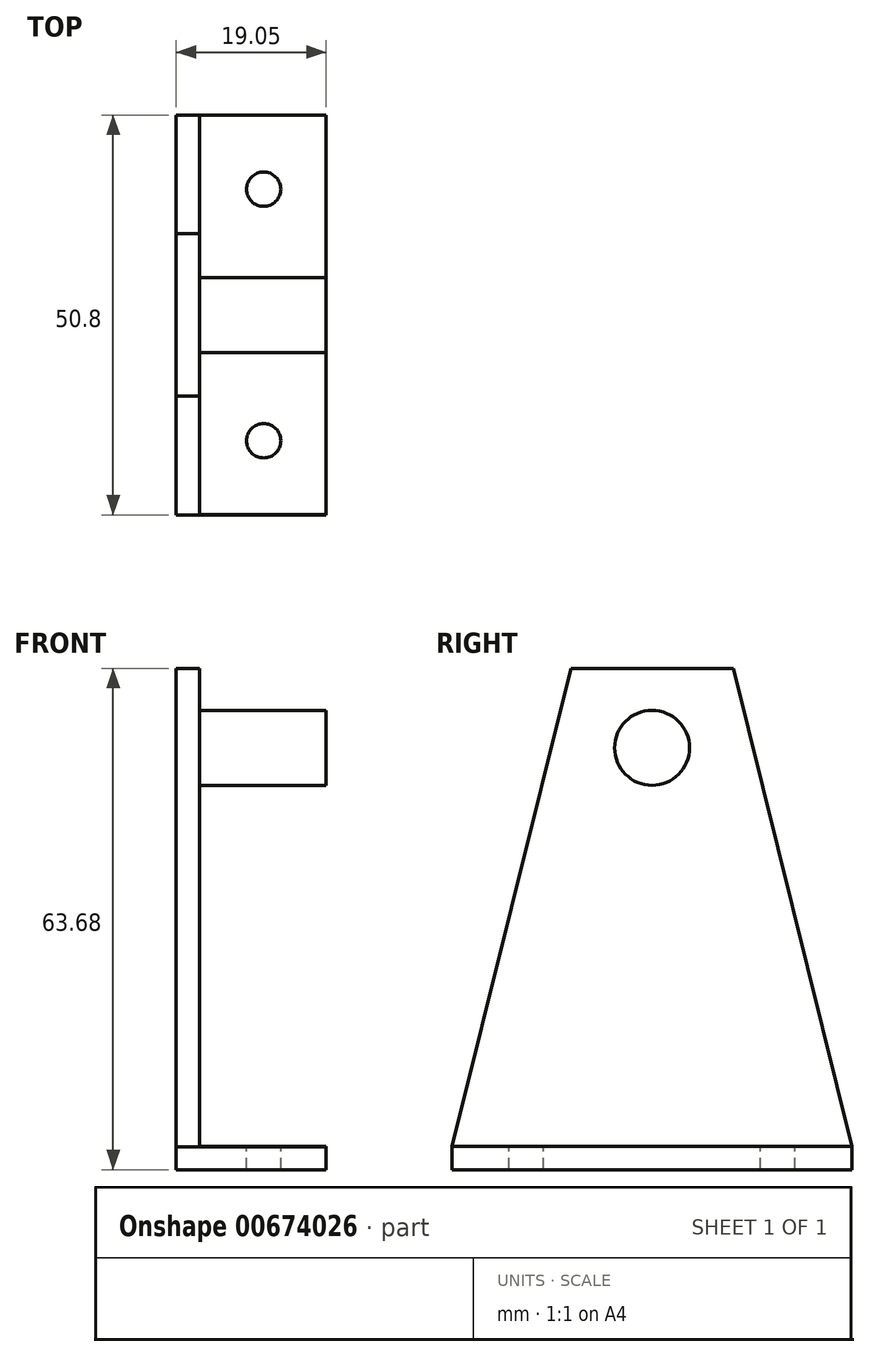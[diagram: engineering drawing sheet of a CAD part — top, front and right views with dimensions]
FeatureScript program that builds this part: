
annotation { "Feature Type Name" : "Feature", "Feature Type Description" : "" }
export const myFeature = defineFeature(function(context is Context, id is Id, definition is map)
    precondition{}
    {
        {
            var Q0;
            Q0=qCreatedBy(makeId("Front.planeOp"),FACE);
            var sketch = newSketch(context, id + "F0", { "sketchPlane" : qUnion([Q0])});
            skLineSegment(sketch, "E0", {"start": v(-9.71, 63.68) * mm, "end": v(-9.71, 0) * mm});
            skLineSegment(sketch, "E1", {"start": v(-9.71, 0) * mm, "end": v(9.34, 0) * mm});
            skLineSegment(sketch, "E2", {"start": v(9.34, 0) * mm, "end": v(9.34, 2.97) * mm});
            skLineSegment(sketch, "E3", {"start": v(9.34, 2.97) * mm, "end": v(-6.74, 2.97) * mm});
            skLineSegment(sketch, "E4", {"start": v(-6.74, 2.97) * mm, "end": v(-6.74, 63.68) * mm});
            skLineSegment(sketch, "E5", {"start": v(-6.74, 63.68) * mm, "end": v(-9.71, 63.68) * mm});
            skLineSegment(sketch, "E6", {"start": v(-6.74, 58.36) * mm, "end": v(9.34, 58.36) * mm});
            skLineSegment(sketch, "E7", {"start": v(9.34, 58.36) * mm, "end": v(9.34, 48.83) * mm});
            skLineSegment(sketch, "E8", {"start": v(9.34, 48.83) * mm, "end": v(-6.74, 48.83) * mm});
            skLineSegment(sketch, "E9", {"start": v(9.34, 53.6) * mm, "end": v(-6.74, 53.6) * mm});
            skSolve(sketch);
        }
        {
            var Q0;
            Q0=makeQuery(id+"F0.imprint","IMPRINT",FACE,{"disambiguationData":[TD([[makeQuery(id+"F0.imprint","IMPRINT",EDGE,{"derivedFrom":sQuery(id+"F0.wireOp",EDGE,"E0")}),1.0]])]});
            extrude(context, id + "F1", {"entities" : qUnion([Q0]), "endBound" : BoundingType.SYMMETRIC, "depth" : 50.8 * mm, "offsetDistance" : 25.4 * mm});
        }
        {
            var Q0;
            {var subQ0=sQuery(id+"F0.wireOp",EDGE,"E6");Q0=makeQuery(id+"F0.imprint","IMPRINT",FACE,{"disambiguationData":[TD([[makeQuery(id+"F0.imprint","IMPRINT",EDGE,{"derivedFrom":subQ0}),-1.0]])]});}
            var Q1;
            Q1=sQuery(id+"F0.wireOp",EDGE,"E9");
            revolve(context, id + "F2", {"operationType" : NewBodyOperationType.ADD, "surfaceOperationType" : NewSurfaceOperationType.ADD, "entities" : qUnion([Q0]), "axis" : qUnion([Q1]), "revolveType" : RevolveType.FULL});
        }
        {
            var Q0;
            Q0=makeQuery(id+"F1.opExtrude","SWEPT_FACE",FACE,{"disambiguationData":[OSD([sQuery(id+"F0.wireOp",EDGE,"E3")])]});
            var sketch = newSketch(context, id + "F3", { "sketchPlane" : qUnion([Q0])});
            skCircle(sketch, "E10", {"center": v(1.4, 15.98) * mm, "radius": 2.18 * mm});
            skCircle(sketch, "E11", {"center": v(1.4, -15.98) * mm, "radius": 2.18 * mm});
            skLineSegment(sketch, "E12", {"start": v(1.4, 15.98) * mm, "end": v(1.4, -15.98) * mm, "construction": true});
            skLineSegment(sketch, "E13.0", {"start": v(9.34, -25.4) * mm, "end": v(9.34, 25.4) * mm});
            skSolve(sketch);
        }
        {
            var Q0;
            Q0=makeQuery(id+"F3.imprint","IMPRINT",FACE,{"disambiguationData":[TD([[makeQuery(id+"F3.imprint","IMPRINT",EDGE,{"derivedFrom":sQuery(id+"F3.wireOp",EDGE,"E10")}),1.0]])]});
            var Q1;
            Q1=makeQuery(id+"F3.imprint","IMPRINT",FACE,{"disambiguationData":[TD([[makeQuery(id+"F3.imprint","IMPRINT",EDGE,{"derivedFrom":sQuery(id+"F3.wireOp",EDGE,"E11")}),1.0]])]});
            extrude(context, id + "F4", {"entities" : qUnion([Q0, Q1]), "operationType" : NewBodyOperationType.REMOVE, "endBound" : BoundingType.UP_TO_NEXT, "oppositeDirection" : true, "depth" : 25.4 * mm, "offsetDistance" : 25.4 * mm});
        }
        {
            var Q0;
            Q0=makeQuery(id+"F1.opExtrude","SWEPT_FACE",FACE,{"disambiguationData":[OSD([sQuery(id+"F0.wireOp",EDGE,"E0")])]});
            var sketch = newSketch(context, id + "F5", { "sketchPlane" : qUnion([Q0])});
            skLineSegment(sketch, "E14", {"start": v(-10.33, 63.68) * mm, "end": v(-25.4, 2.9) * mm});
            skLineSegment(sketch, "E15", {"start": v(10.33, 63.68) * mm, "end": v(25.4, 2.9) * mm});
            skLineSegment(sketch, "E16", {"start": v(-10.33, 63.68) * mm, "end": v(10.33, 63.68) * mm});
            skSolve(sketch);
        }
        {
            var Q0;
            {var subQ0=sQuery(id+"F5.wireOp",EDGE,"E15");Q0=makeQuery(id+"F5.imprint","IMPRINT",FACE,{"disambiguationData":[TD([[makeQuery(id+"F5.imprint","IMPRINT",EDGE,{"derivedFrom":subQ0}),1.0]])]});}
            var Q1;
            {var subQ0=sQuery(id+"F5.wireOp",EDGE,"E14");Q1=makeQuery(id+"F5.imprint","IMPRINT",FACE,{"disambiguationData":[TD([[makeQuery(id+"F5.imprint","IMPRINT",EDGE,{"derivedFrom":subQ0}),-1.0]])]});}
            extrude(context, id + "F6", {"entities" : qUnion([Q0, Q1]), "operationType" : NewBodyOperationType.REMOVE, "endBound" : BoundingType.THROUGH_ALL, "oppositeDirection" : true, "depth" : 25.4 * mm, "offsetDistance" : 25.4 * mm});
        }
    });
